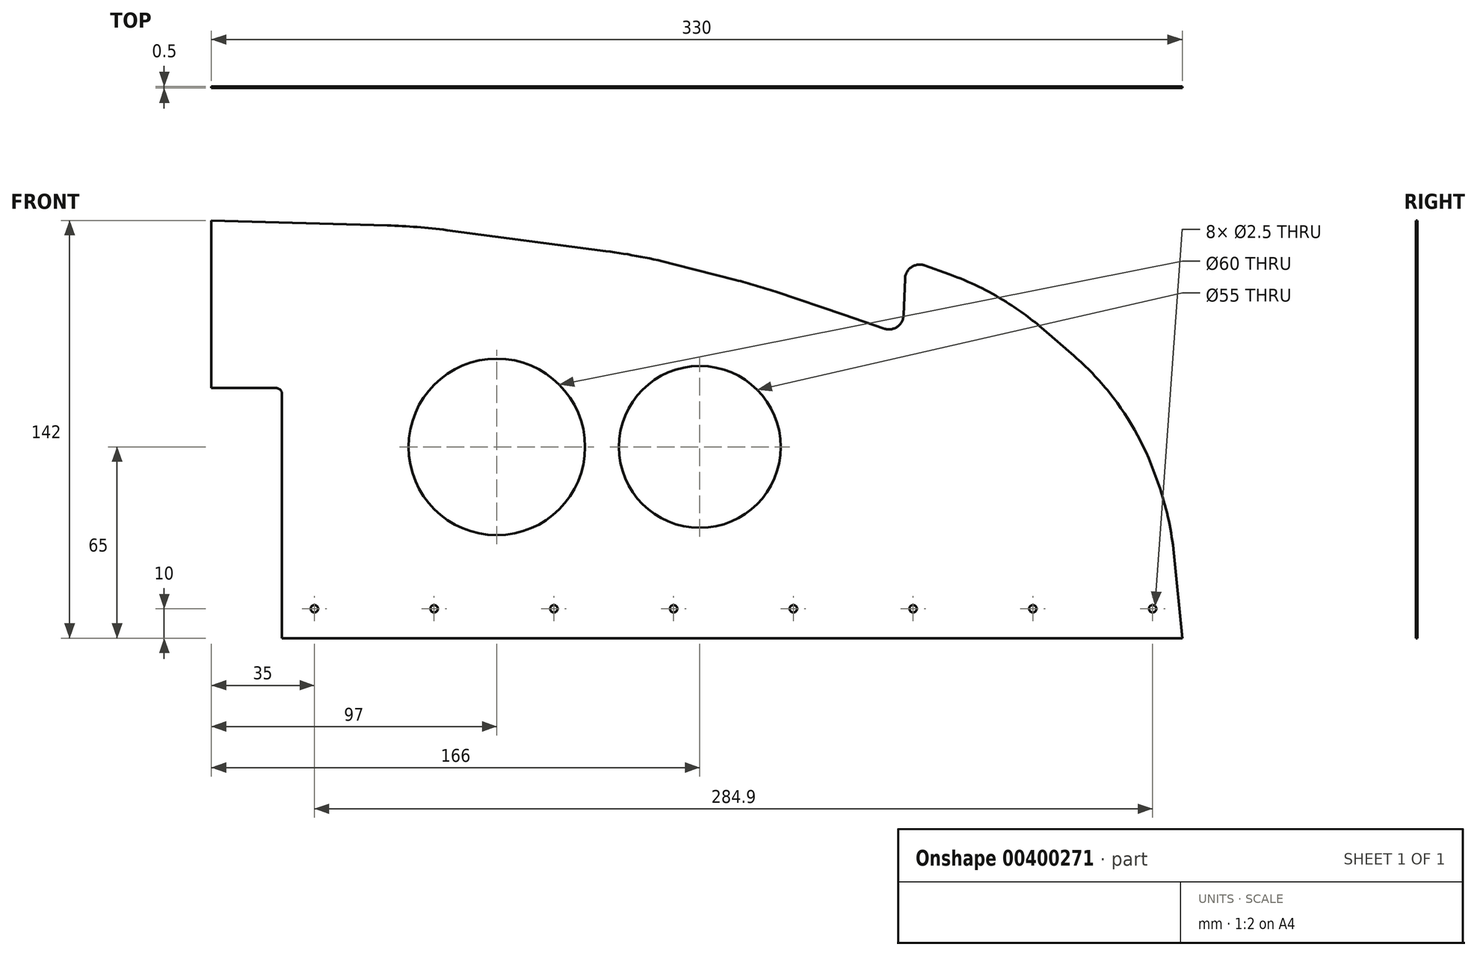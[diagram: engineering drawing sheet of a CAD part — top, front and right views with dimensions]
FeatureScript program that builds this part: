
annotation { "Feature Type Name" : "Feature", "Feature Type Description" : "" }
export const myFeature = defineFeature(function(context is Context, id is Id, definition is map)
    precondition{}
    {
        {
            var Q0;
            Q0=qCreatedBy(makeId("Front.planeOp"),FACE);
            var sketch = newSketch(context, id + "F0", { "sketchPlane" : qUnion([Q0])});
            skLineSegment(sketch, "E0", {"start": v(24, 0) * mm, "end": v(330, 0) * mm});
            skLineSegment(sketch, "E1", {"start": v(330, 0) * mm, "end": v(326, 40) * mm});
            skLineSegment(sketch, "E2", {"start": v(326, 40) * mm, "end": v(316, 70) * mm});
            skLineSegment(sketch, "E3", {"start": v(316, 70) * mm, "end": v(300, 90) * mm});
            skLineSegment(sketch, "E4", {"start": v(300, 90) * mm, "end": v(277, 110) * mm});
            skLineSegment(sketch, "E5", {"start": v(277, 110) * mm, "end": v(261, 120) * mm});
            skLineSegment(sketch, "E6", {"start": v(261, 120) * mm, "end": v(236, 129) * mm});
            skLineSegment(sketch, "E7", {"start": v(146, 130) * mm, "end": v(70, 140) * mm});
            skLineSegment(sketch, "E8", {"start": v(70, 140) * mm, "end": v(0, 142) * mm});
            skLineSegment(sketch, "E9", {"start": v(0, 142) * mm, "end": v(0, 85) * mm});
            skLineSegment(sketch, "E10", {"start": v(0, 85) * mm, "end": v(24, 85) * mm});
            skLineSegment(sketch, "E11", {"start": v(24, 85) * mm, "end": v(24, 0) * mm});
            skPoint(sketch, "E12.orphan", {"position": v(0, 0) * mm});
            skLineSegment(sketch, "E13", {"start": v(236, 129) * mm, "end": v(235, 103) * mm});
            skLineSegment(sketch, "E14", {"start": v(235, 103) * mm, "end": v(215, 110) * mm});
            skLineSegment(sketch, "E15", {"start": v(215, 110) * mm, "end": v(185, 120) * mm});
            skLineSegment(sketch, "E16", {"start": v(0, 0) * mm, "end": v(0, 159.06) * mm, "construction": true});
            skLineSegment(sketch, "E17", {"start": v(185, 120) * mm, "end": v(146, 130) * mm});
            skCircle(sketch, "E18", {"center": v(35, 10) * mm, "radius": 1.25 * mm});
            skCircle(sketch, "E19.1.0.0", {"center": v(75.7, 10) * mm, "radius": 1.25 * mm});
            skCircle(sketch, "E19.2.0.0", {"center": v(116.4, 10) * mm, "radius": 1.25 * mm});
            skCircle(sketch, "E19.3.0.0", {"center": v(157.1, 10) * mm, "radius": 1.25 * mm});
            skCircle(sketch, "E19.4.0.0", {"center": v(197.8, 10) * mm, "radius": 1.25 * mm});
            skCircle(sketch, "E19.5.0.0", {"center": v(238.5, 10) * mm, "radius": 1.25 * mm});
            skCircle(sketch, "E19.6.0.0", {"center": v(279.2, 10) * mm, "radius": 1.25 * mm});
            skCircle(sketch, "E19.7.0.0", {"center": v(319.9, 10) * mm, "radius": 1.25 * mm});
            skLineSegment(sketch, "E19.direction1", {"start": v(35, 10) * mm, "end": v(75.7, 10) * mm, "construction": true});
            skCircle(sketch, "E20", {"center": v(97, 65) * mm, "radius": 30 * mm});
            skCircle(sketch, "E21", {"center": v(166, 65) * mm, "radius": 27.5 * mm});
            skSolve(sketch);
        }
        {
            var Q0;
            Q0=makeQuery(id+"F0.imprint","IMPRINT",FACE,{"disambiguationData":[TD([[makeQuery(id+"F0.imprint","IMPRINT",EDGE,{"derivedFrom":sQuery(id+"F0.wireOp",EDGE,"E0")}),1.0]])]});
            extrude(context, id + "F1", {"entities" : qUnion([Q0]), "depth" : 0.5 * mm, "offsetDistance" : 25 * mm});
        }
        {
            var Q0;
            Q0=makeQuery(id+"F1.opExtrude","SWEPT_EDGE",EDGE,{"disambiguationData":[OSD([sQuery(id+"F0.wireOp",EDGE,"E10"),sQuery(id+"F0.wireOp",EDGE,"E11")])]});
            fillet(context, id + "F2", {"entities" : qUnion([Q0]), "tangentPropagation" : true, "radius" : 2 * mm, "defaultsChanged" : true, "vertexSettings" : [], "allowEdgeOverflow" : false});
        }
        {
            var Q0;
            Q0=makeQuery(id+"F1.opExtrude","SWEPT_EDGE",EDGE,{"disambiguationData":[OSD([sQuery(id+"F0.wireOp",EDGE,"E13"),sQuery(id+"F0.wireOp",EDGE,"E14")])]});
            var Q1;
            Q1=makeQuery(id+"F1.opExtrude","SWEPT_EDGE",EDGE,{"disambiguationData":[OSD([sQuery(id+"F0.wireOp",EDGE,"E6"),sQuery(id+"F0.wireOp",EDGE,"E13")])]});
            fillet(context, id + "F3", {"entities" : qUnion([Q0, Q1]), "tangentPropagation" : true, "radius" : 5 * mm, "defaultsChanged" : false, "vertexSettings" : [], "allowEdgeOverflow" : false});
        }
        {
            var Q0;
            Q0=makeQuery(id+"F1.opExtrude","SWEPT_EDGE",EDGE,{"disambiguationData":[OSD([sQuery(id+"F0.wireOp",EDGE,"E7"),sQuery(id+"F0.wireOp",EDGE,"E8")])]});
            var Q1;
            Q1=makeQuery(id+"F1.opExtrude","SWEPT_EDGE",EDGE,{"disambiguationData":[OSD([sQuery(id+"F0.wireOp",EDGE,"E7"),sQuery(id+"F0.wireOp",EDGE,"E17")])]});
            fillet(context, id + "F4", {"entities" : qUnion([Q0, Q1]), "tangentPropagation" : true, "radius" : 200 * mm, "defaultsChanged" : false, "vertexSettings" : [], "allowEdgeOverflow" : false});
        }
        {
            var Q0;
            Q0=makeQuery(id+"F1.opExtrude","SWEPT_EDGE",EDGE,{"disambiguationData":[OSD([sQuery(id+"F0.wireOp",EDGE,"E15"),sQuery(id+"F0.wireOp",EDGE,"E17")])]});
            fillet(context, id + "F5", {"entities" : qUnion([Q0]), "tangentPropagation" : true, "radius" : 200 * mm, "defaultsChanged" : true, "vertexSettings" : [], "allowEdgeOverflow" : false});
        }
        {
            var Q0;
            Q0=makeQuery(id+"F1.opExtrude","SWEPT_EDGE",EDGE,{"disambiguationData":[OSD([sQuery(id+"F0.wireOp",EDGE,"E1"),sQuery(id+"F0.wireOp",EDGE,"E2")])]});
            var Q1;
            Q1=makeQuery(id+"F1.opExtrude","SWEPT_EDGE",EDGE,{"disambiguationData":[OSD([sQuery(id+"F0.wireOp",EDGE,"E2"),sQuery(id+"F0.wireOp",EDGE,"E3")])]});
            var Q2;
            Q2=makeQuery(id+"F1.opExtrude","SWEPT_EDGE",EDGE,{"disambiguationData":[OSD([sQuery(id+"F0.wireOp",EDGE,"E3"),sQuery(id+"F0.wireOp",EDGE,"E4")])]});
            var Q3;
            Q3=makeQuery(id+"F1.opExtrude","SWEPT_EDGE",EDGE,{"disambiguationData":[OSD([sQuery(id+"F0.wireOp",EDGE,"E4"),sQuery(id+"F0.wireOp",EDGE,"E5")])]});
            var Q4;
            Q4=makeQuery(id+"F1.opExtrude","SWEPT_EDGE",EDGE,{"disambiguationData":[OSD([sQuery(id+"F0.wireOp",EDGE,"E5"),sQuery(id+"F0.wireOp",EDGE,"E6")])]});
            fillet(context, id + "F6", {"entities" : qUnion([Q0, Q1, Q2, Q3, Q4]), "tangentPropagation" : true, "radius" : 100 * mm, "defaultsChanged" : false, "vertexSettings" : [], "allowEdgeOverflow" : false});
        }
    });
